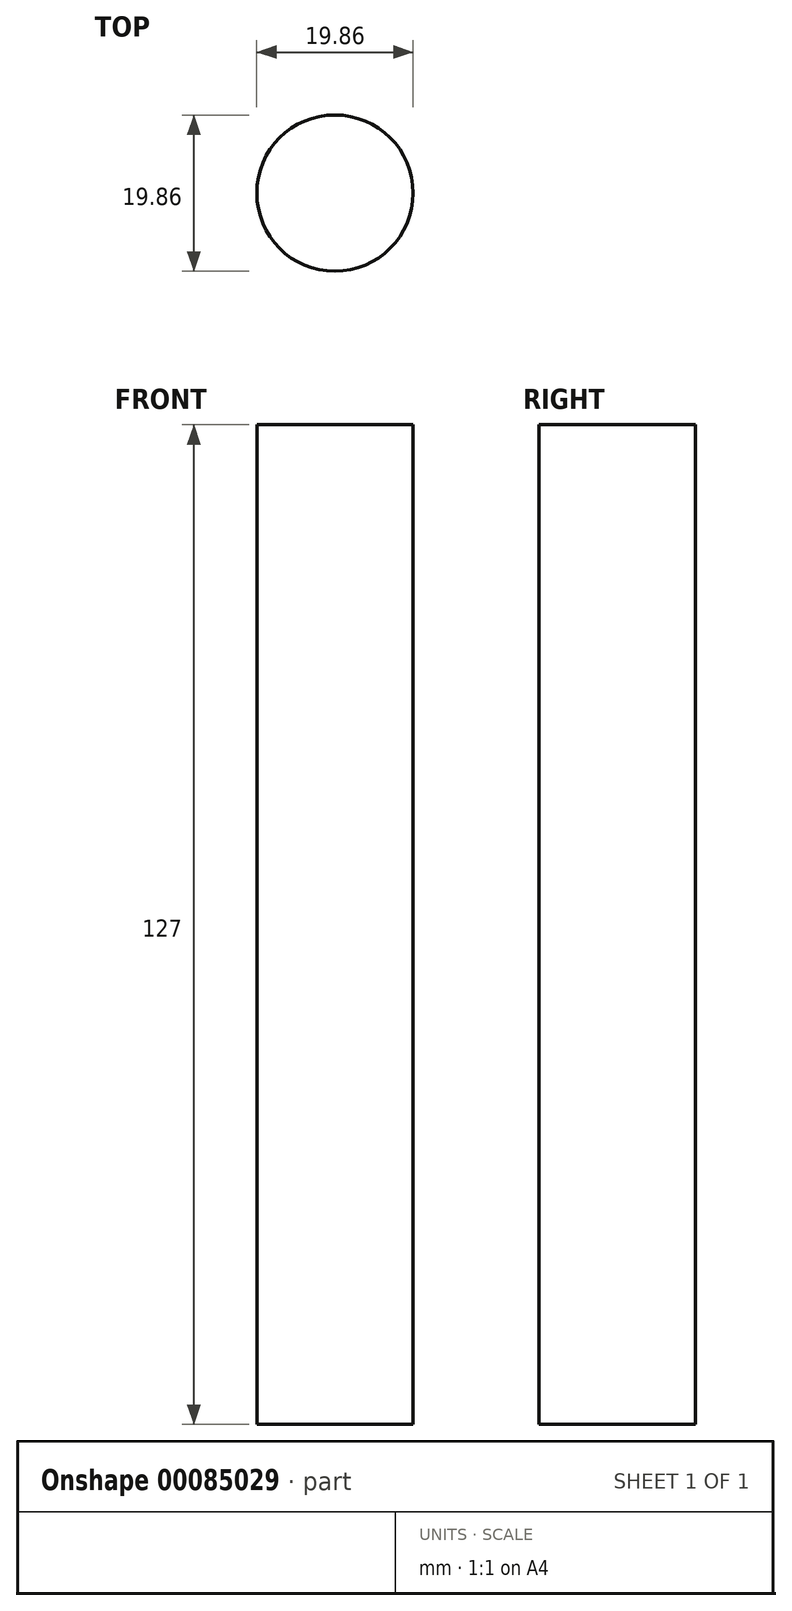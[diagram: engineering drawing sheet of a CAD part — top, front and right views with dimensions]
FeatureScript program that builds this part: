
annotation { "Feature Type Name" : "Feature", "Feature Type Description" : "" }
export const myFeature = defineFeature(function(context is Context, id is Id, definition is map)
    precondition{}
    {
        {
            var Q0;
            Q0=qCreatedBy(makeId("Top.planeOp"),FACE);
            var sketch = newSketch(context, id + "F0", { "sketchPlane" : qUnion([Q0])});
            skCircle(sketch, "E0", {"center": v(-15.09, 7.77) * mm, "radius": 9.93 * mm});
            skSolve(sketch);
        }
        {
            var Q0;
            Q0=makeQuery(id+"F0.imprint","IMPRINT",FACE,{"disambiguationData":[TD([[makeQuery(id+"F0.imprint","IMPRINT",EDGE,{"derivedFrom":sQuery(id+"F0.wireOp",EDGE,"E0")}),1.0]])]});
            extrude(context, id + "F1", {"entities" : qUnion([Q0]), "depth" : 127 * mm});
        }
    });
